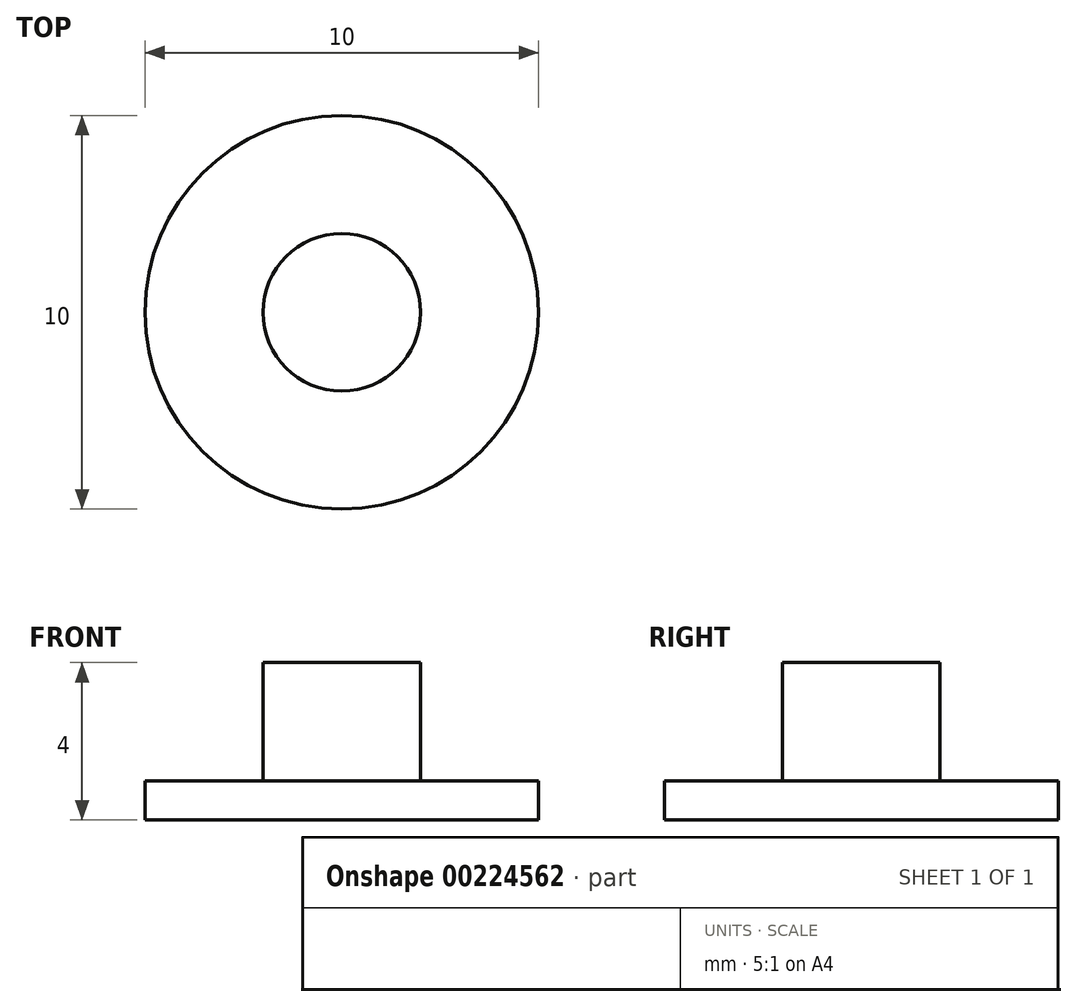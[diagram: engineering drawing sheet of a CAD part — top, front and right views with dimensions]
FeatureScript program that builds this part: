
annotation { "Feature Type Name" : "Feature", "Feature Type Description" : "" }
export const myFeature = defineFeature(function(context is Context, id is Id, definition is map)
    precondition{}
    {
        {
            var Q0;
            Q0=qCreatedBy(makeId("Front.planeOp"),FACE);
            var sketch = newSketch(context, id + "F0", { "sketchPlane" : qUnion([Q0])});
            skLineSegment(sketch, "E0", {"start": v(0, 4) * mm, "end": v(2, 4) * mm});
            skLineSegment(sketch, "E1", {"start": v(2, 4) * mm, "end": v(2, 1) * mm});
            skLineSegment(sketch, "E2", {"start": v(2, 1) * mm, "end": v(5, 1) * mm});
            skLineSegment(sketch, "E3", {"start": v(5, 1) * mm, "end": v(5, 0) * mm});
            skLineSegment(sketch, "E4", {"start": v(5, 0) * mm, "end": v(0, 0) * mm});
            skLineSegment(sketch, "E5", {"start": v(0, 0) * mm, "end": v(0, 4) * mm});
            skSolve(sketch);
        }
        {
            var Q0;
            Q0 = qSketchRegion(id + "F0", true);
            var Q1;
            Q1=sQuery(id+"F0.wireOp",EDGE,"E5");
            revolve(context, id + "F1", {"entities" : qUnion([Q0]), "axis" : qUnion([Q1]), "revolveType" : RevolveType.FULL});
        }
    });
